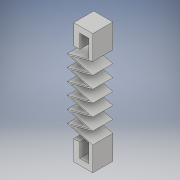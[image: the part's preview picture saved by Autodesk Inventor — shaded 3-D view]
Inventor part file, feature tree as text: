
AUTODESK INVENTOR PART (.ipt)
format: ipt  version: 2019 (Build 230136000, 136)  size: 151,552 bytes
history: native  units: in
note: dims shown in document units (in); Inventor stores cm internally (conversion verified against a paired STEP export)
features: extrude x1, sketch x1
ambient origin geometry x8: Origin, YZ Plane, XZ Plane, XY Plane, X Axis, Y Axis, Z Axis, Center Point
bodies: Body1 (feature_tree)
feature tree (2):
  extrude  "Extrusion2"  Depth=0.1969in
  sketch  "Sketch2"  dims[d9=0.3937in d14=0.1969in d15=0.0591in d16=0.187in d17=0.2362in d18=0.1378in d19=0.0886in d24=0.1772in d25=0.1181in d28=0.0591in d29=0.0in d37=0.107in d38=0.5906in d39=0.1206in d40=0.0467in d41=0.1969in d42=0.0in]
